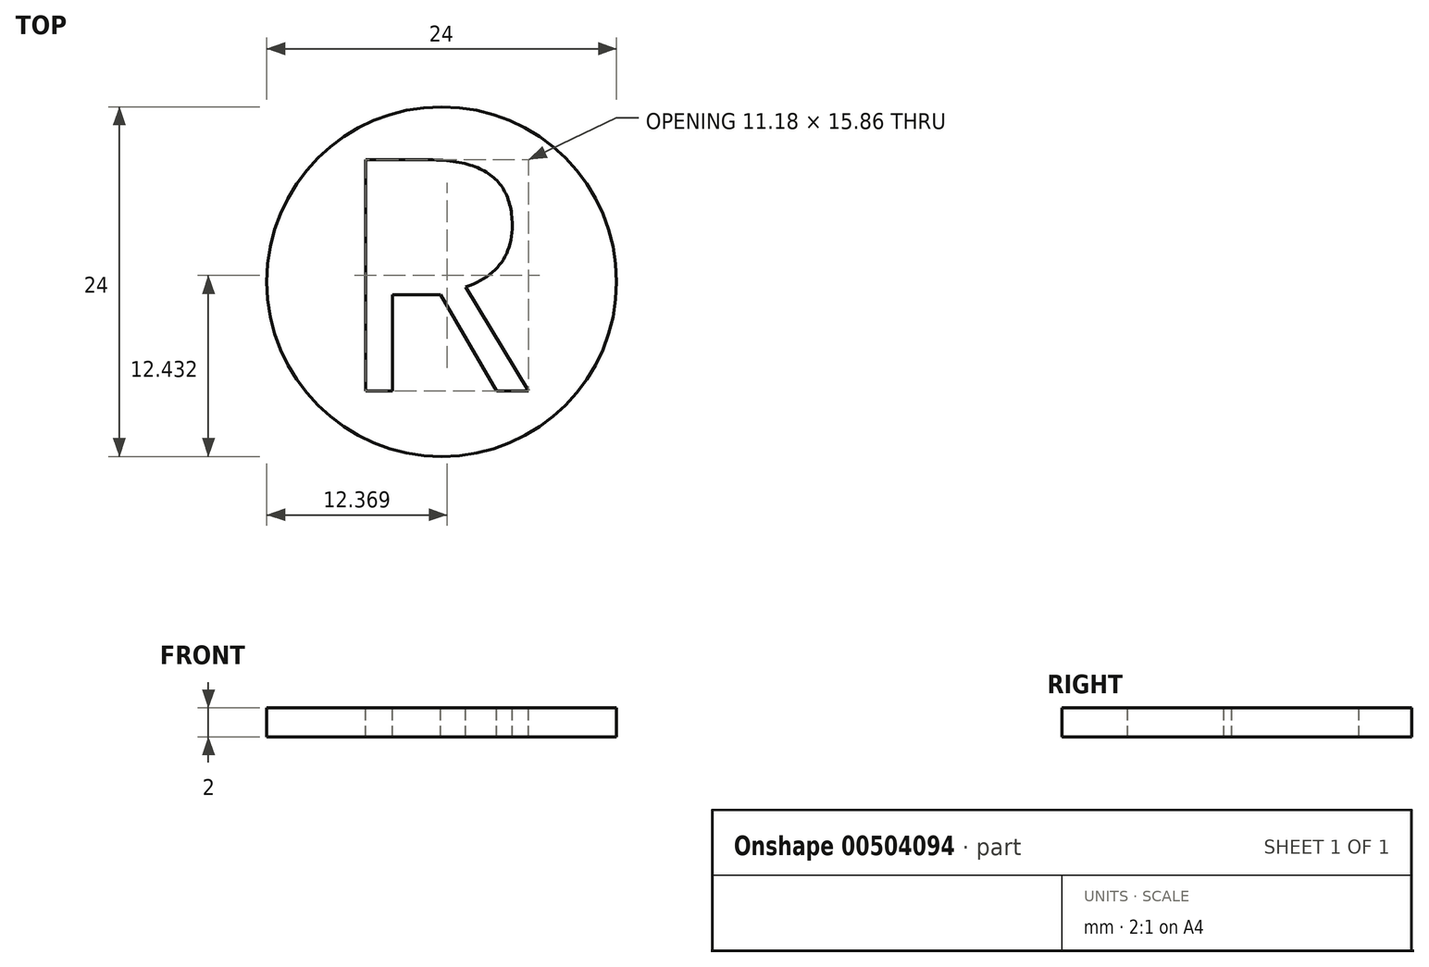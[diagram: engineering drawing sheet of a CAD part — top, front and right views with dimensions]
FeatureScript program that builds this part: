
annotation { "Feature Type Name" : "Feature", "Feature Type Description" : "" }
export const myFeature = defineFeature(function(context is Context, id is Id, definition is map)
    precondition{}
    {
        {
            var Q0;
            Q0=qCreatedBy(makeId("Top.planeOp"),FACE);
            var sketch = newSketch(context, id + "F0", { "sketchPlane" : qUnion([Q0])});
            skCircle(sketch, "E0", {"center": v(0, 0) * mm, "radius": 12 * mm});
            skSolve(sketch);
        }
        {
            var Q0;
            Q0=qSketchRegion(id+"F0",true);
            extrude(context, id + "F1", {"entities" : qUnion([Q0]), "depth" : 2 * mm});
        }
        {
            var Q0;
            Q0=makeQuery(id+"F1.opExtrude","CAP_FACE",FACE,{"disambiguationData":[OSD([sQuery(id+"F0.wireOp",EDGE,"E0")])],"isStart":false});
            var sketch = newSketch(context, id + "F2", { "sketchPlane" : qUnion([Q0])});
            skPoint(sketch, "E1", {"position": v(0, 12) * mm});
            skText(sketch, "E2", { "text": "R", "fontName": "OpenSans-Regular.ttf"});
            skPoint(sketch, "E3", {"position": v(0, 9) * mm});
            const initialGuessF2  = {"E2": [-0.0074, -0.0075, 1, 0, 0.016]};
            skSetInitialGuess(sketch, initialGuessF2);
            skSolve(sketch);
        }
        {
            var Q0;
            {var subQ6=sQuery(id+"F2.wireOp",EDGE,"E2.sketch_text.stroke-1");Q0=makeQuery(id+"F2.imprint","IMPRINT",FACE,{"disambiguationData":[TD([[makeQuery(id+"F2.imprint","IMPRINT",EDGE,{"derivedFrom":subQ6}),-1.0]])]});}
            var Q1;
            Q1=makeQuery(id+"F2.imprint","IMPRINT",FACE,{"disambiguationData":[TD([[makeQuery(id+"F2.imprint","IMPRINT",EDGE,{"derivedFrom":sQuery(id+"F2.wireOp",EDGE,"E2.sketch_text.stroke-11")}),1.0]])]});
            extrude(context, id + "F3", {"entities" : qUnion([Q0, Q1]), "operationType" : NewBodyOperationType.REMOVE, "oppositeDirection" : true, "depth" : 25 * mm});
        }
    });
